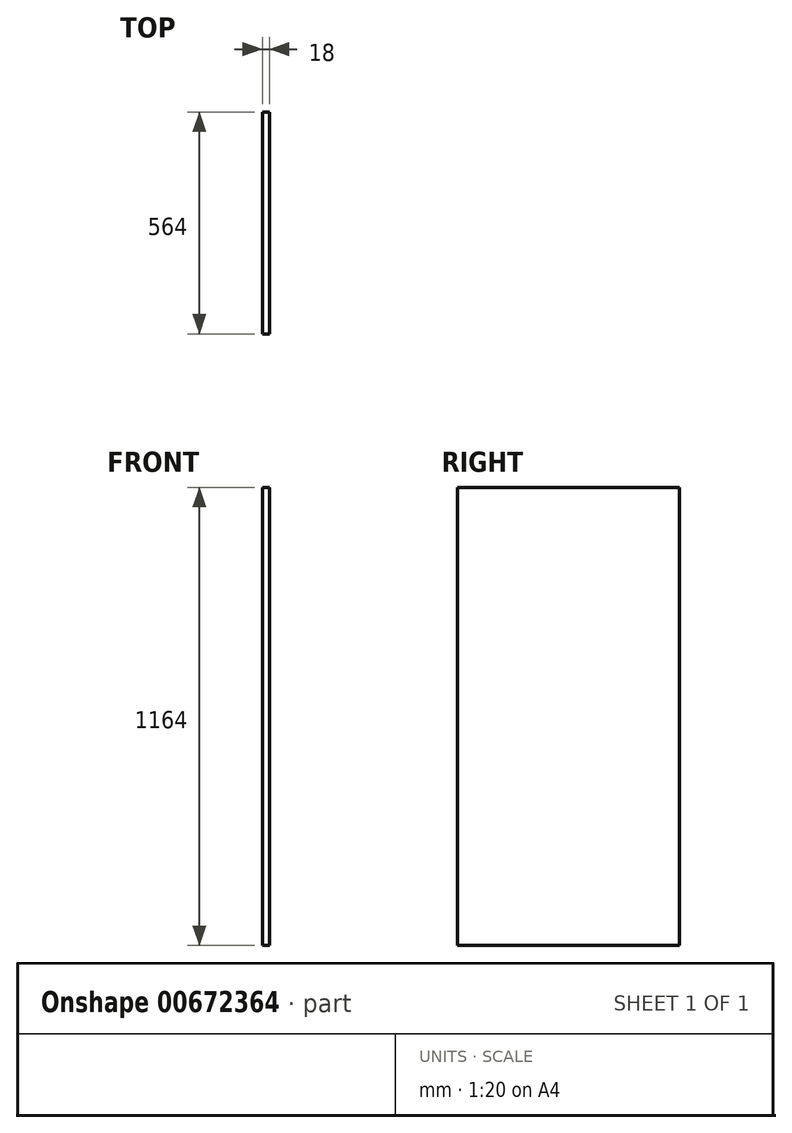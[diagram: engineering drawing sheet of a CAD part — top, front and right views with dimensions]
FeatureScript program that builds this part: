
annotation { "Feature Type Name" : "Feature", "Feature Type Description" : "" }
export const myFeature = defineFeature(function(context is Context, id is Id, definition is map)
    precondition{}
    {
        {
            var Q0;
            Q0=qCreatedBy(makeId("Right.planeOp"),FACE);
            var sketch = newSketch(context, id + "F0", { "sketchPlane" : qUnion([Q0])});
            skLineSegment(sketch, "E0.bottom", {"start": v(0, 0) * mm, "end": v(564, 0) * mm});
            skLineSegment(sketch, "E0.top", {"start": v(0, 1164) * mm, "end": v(564, 1164) * mm});
            skLineSegment(sketch, "E0.left", {"start": v(0, 0) * mm, "end": v(0, 1164) * mm});
            skLineSegment(sketch, "E0.right", {"start": v(564, 0) * mm, "end": v(564, 1164) * mm});
            skSolve(sketch);
        }
        {
            var Q0;
            Q0=makeQuery(id+"F0.imprint","IMPRINT",FACE,{"disambiguationData":[TD([[makeQuery(id+"F0.imprint","IMPRINT",EDGE,{"derivedFrom":sQuery(id+"F0.wireOp",EDGE,"E0.bottom")}),1.0]])]});
            extrude(context, id + "F1", {"entities" : qUnion([Q0]), "depth" : 18 * mm, "offsetDistance" : 25 * mm});
        }
    });
